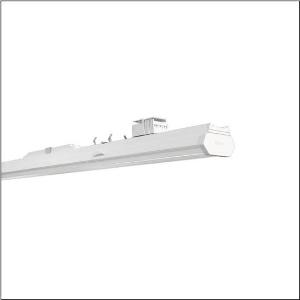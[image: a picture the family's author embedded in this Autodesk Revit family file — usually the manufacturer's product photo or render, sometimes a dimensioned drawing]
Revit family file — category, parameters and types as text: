
# Revit family: licross_11_protected_mo_51td1bdn49xg3s
name_source: partatom
category: Lighting Fixtures
units: mm (PartAtom-declared; Revit-internal decimal feet)

## family parameters
Cut with Voids When Loaded = No
Host = Face
Light Source = No
Part Type = Normal
Room Calculation Point = No
Round Connector Dimension = Use Diameter
Shared = No

## types (1)
- --- (1 x LED, 920 lm, 6.8 W, 4000K)
    Apparent Load = 7 VA
    CIE Flux Codes = 54 82 95 97 100
    Color Rendering = 80
    Color Temperature = 4000K
    Default Elevation = 1800 mm
    Description = Licross 11 Protected MO, luminaire insert, of sheet steel, galvanised, coil coated, white, length: 1.500mm, width: 90mm, height: 101mm, LED rated luminous flux: 9.370lm, light colour: 840, SDCM (Standard Deviation of Colour Matching)MacAdam ≤ 2 SDCM (initial), control gear: DALI 2 (for two DALI lines), with plug, 6-pole, with phase selection, for trunking rail, 14-core, mains connection: 220..240V, AC, 50/60Hz, rated input power: 61W, for trunking rail, 14-core, internal wiring halogen-free, for emergency light function, converter,control gear: single battery element, battery: LiFePO4, 9Ah, primary optical cover: cover, of PMMA, light emission: direct distribution, primary light characteristic: symmetric, protection rating (complete): IP54, insulation class (complete): insulation class I (protective earthing), certification: CE, UKCA, protection symbol: D if used in an environment with non-conductive dust loads with corresponding accessories, impact resistance: IK06, permissible ambient temperature for indoor applications: +5..+35°C, standard: EN 60598-2-22, LABS conformity tested according to VDMA 24364:2018-05, reducing of maximum allowable ambient temperature of 5°C with ceiling mounting, corresponds to IFS (International Featured Standards) requirements for safety and quality in the food industry, The light source and the operating device comply with the requirements of the Ecodesign Regulation (EU) 2019/2020 and are replaceable in accordance with this regulation, packaging unit: 1 piece
    Height = 92 mm
    Lamp = 1 x LED
    Lamp Light Flux = 920 lm
    Lamp Power = 6.8 W
    Lamp count = 1
    Length = 1500 mm
    Luminous efficacy = 135 lm/W
    Manufacturer = Siteco
    ModVariant = No
    Model = 51TD1BDN49XG3S
    Mounting Place = Ceiling
    Mounting Type = Pendant
    Number of Poles = 1
    OnlyDefault = Yes
    Power Factor = 1
    Product Name = Licross 11 Protected MO
    Product group = luminaire insert | ceiling pendant
    ProductGroupID = 901
    Protection Class = Protection class I
    Protection Degree = IP 54
    RLX_Detail_Level = 1
    RLX_Emergency_Light_Flux = 0 lm
    RLX_Emergency_Type = 0
    RLX_Emergency_Type_DB = No
    RlxData = <blob elided: 24993 chars, md5=4c11bd93>
    Socket = socket
    Standby Power = 0 W
    System Light Flux = 920 lm
    System Power = 7 W
    Type Comments = : emergency light operation: 3 h
    Type Image = l_1256145.jpg
    URL = http://relux.com
    VarID = @adj_096607
    Voltage = 0 V
    Weight = 0.00 kg
    Width = 88 mm

## geometry (parser evidence)
native form markers: Blend x4, Sweep x10
no freeform markers — native parametric forms only
